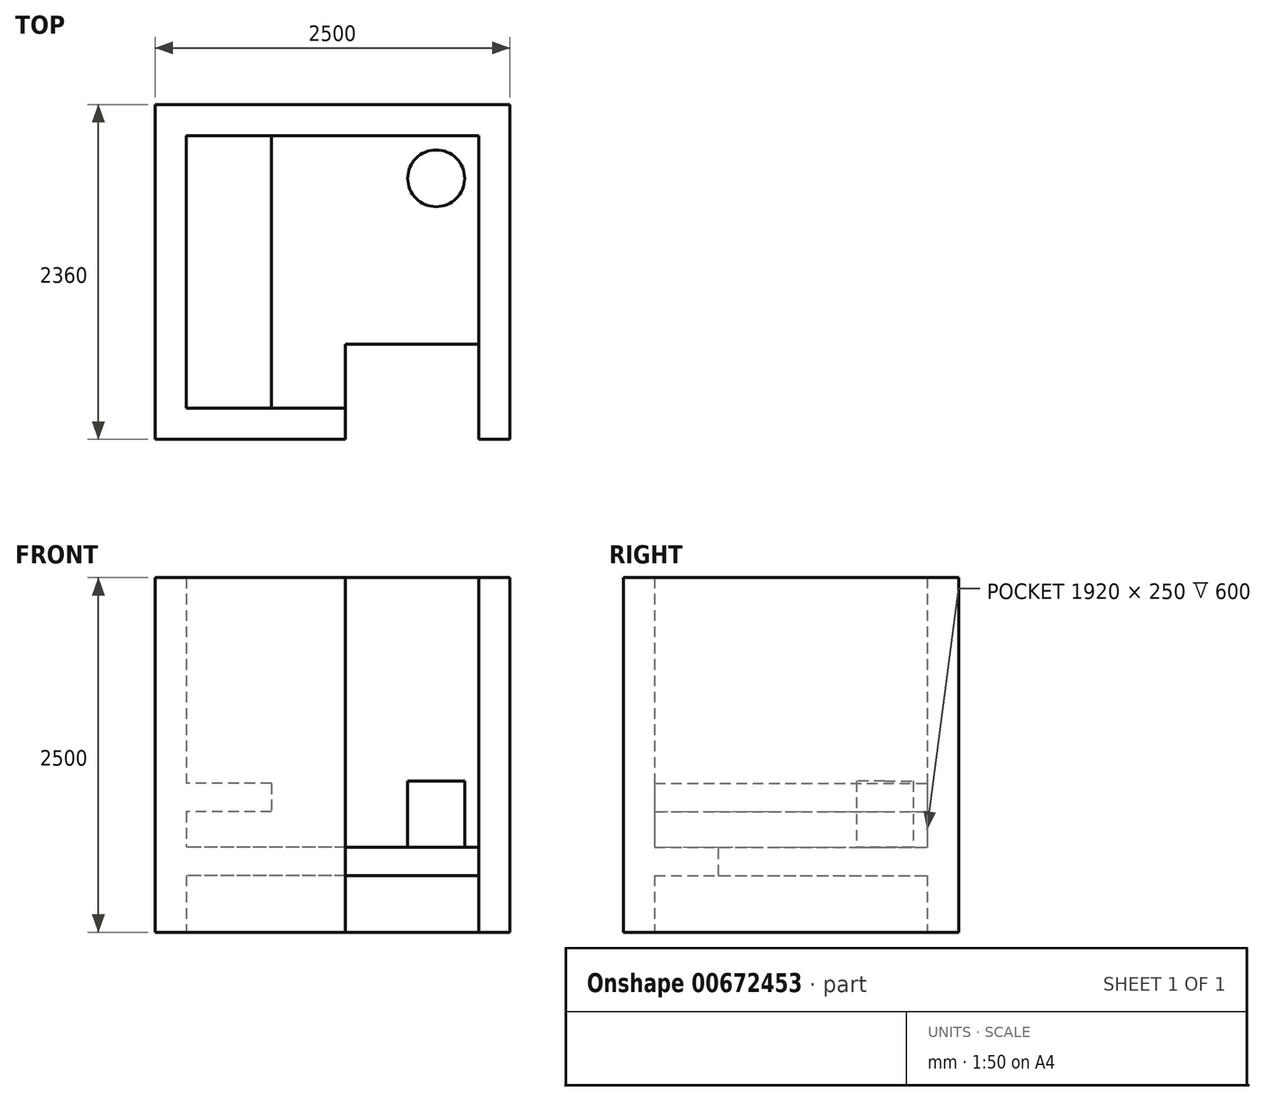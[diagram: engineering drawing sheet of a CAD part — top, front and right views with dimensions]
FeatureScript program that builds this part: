
annotation { "Feature Type Name" : "Feature", "Feature Type Description" : "" }
export const myFeature = defineFeature(function(context is Context, id is Id, definition is map)
    precondition{}
    {
        {
            var Q0;
            Q0=qCreatedBy(makeId("Top.planeOp"),FACE);
            var sketch = newSketch(context, id + "F0", { "sketchPlane" : qUnion([Q0])});
            skLineSegment(sketch, "E0.bottom", {"start": v(1030, 960) * mm, "end": v(-1030, 960) * mm});
            skLineSegment(sketch, "E0.top", {"start": v(90, -960) * mm, "end": v(-1030, -960) * mm});
            skLineSegment(sketch, "E0.left", {"start": v(1030, 960) * mm, "end": v(1030, -960) * mm});
            skLineSegment(sketch, "E0.right", {"start": v(-1030, 960) * mm, "end": v(-1030, -960) * mm});
            skPoint(sketch, "E0.middle", {"position": v(0, 0) * mm});
            skLineSegment(sketch, "E1.0", {"start": v(1250, 1180) * mm, "end": v(-1250, 1180) * mm});
            skLineSegment(sketch, "E1.1", {"start": v(1250, 1180) * mm, "end": v(1250, -1180) * mm});
            skLineSegment(sketch, "E1.2", {"start": v(1250, -1180) * mm, "end": v(1030, -1180) * mm});
            skLineSegment(sketch, "E1.3", {"start": v(-1250, 1180) * mm, "end": v(-1250, -1180) * mm});
            skLineSegment(sketch, "E2", {"start": v(1030, -960) * mm, "end": v(1030, -1180) * mm});
            skLineSegment(sketch, "E3", {"start": v(90, -960) * mm, "end": v(90, -1180) * mm});
            skLineSegment(sketch, "E4.trimOffspring", {"start": v(90, -1180) * mm, "end": v(-1250, -1180) * mm});
            skSolve(sketch);
        }
        {
            var Q0;
            Q0=makeQuery(id+"F0.imprint","IMPRINT",FACE,{"disambiguationData":[TD([[makeQuery(id+"F0.imprint","IMPRINT",EDGE,{"derivedFrom":sQuery(id+"F0.wireOp",EDGE,"E0.bottom")}),-1.0]])]});
            extrude(context, id + "F1", {"entities" : qUnion([Q0]), "depth" : 2500 * mm, "offsetDistance" : 25 * mm});
        }
        {
            var Q0;
            Q0=makeQuery(id+"F1.opExtrude","SWEPT_FACE",FACE,{"disambiguationData":[OSD([sQuery(id+"F0.wireOp",EDGE,"E0.bottom")])]});
            var sketch = newSketch(context, id + "F2", { "sketchPlane" : qUnion([Q0])});
            skLineSegment(sketch, "E5.bottom", {"start": v(1030, 600) * mm, "end": v(-1030, 600) * mm});
            skLineSegment(sketch, "E5.top", {"start": v(1030, 400) * mm, "end": v(-1030, 400) * mm});
            skLineSegment(sketch, "E5.left", {"start": v(1030, 600) * mm, "end": v(1030, 400) * mm});
            skLineSegment(sketch, "E5.right", {"start": v(-1030, 600) * mm, "end": v(-1030, 400) * mm});
            skSolve(sketch);
        }
        {
            var Q0;
            Q0=makeQuery(id+"F2.imprint","IMPRINT",FACE,{"disambiguationData":[TD([[makeQuery(id+"F2.imprint","IMPRINT",EDGE,{"derivedFrom":sQuery(id+"F2.wireOp",EDGE,"E5.bottom")}),1.0]])]});
            extrude(context, id + "F3", {"entities" : qUnion([Q0]), "operationType" : NewBodyOperationType.ADD, "depth" : 1920 * mm, "offsetDistance" : 25 * mm});
        }
        {
            var Q0;
            {var subQ1=sQuery(id+"F0.wireOp",EDGE,"E0.right");Q0=makeQuery(id+"F3.boolean.opBoolean","SPLIT",FACE,{"disambiguationData":[TD([makeQuery(id+"F3.opExtrude","SWEPT_FACE",FACE,{"disambiguationData":[OSD([sQuery(id+"F2.wireOp",EDGE,"E5.bottom")])]})])],"derivedFrom":makeQuery(id+"F1.opExtrude","SWEPT_FACE",FACE,{"disambiguationData":[OSD([subQ1])]})});}
            var sketch = newSketch(context, id + "F4", { "sketchPlane" : qUnion([Q0])});
            skLineSegment(sketch, "E6.bottom", {"start": v(-960, 1050) * mm, "end": v(960, 1050) * mm});
            skLineSegment(sketch, "E6.top", {"start": v(-960, 850) * mm, "end": v(960, 850) * mm});
            skLineSegment(sketch, "E6.left", {"start": v(-960, 1050) * mm, "end": v(-960, 850) * mm});
            skLineSegment(sketch, "E6.right", {"start": v(960, 1050) * mm, "end": v(960, 850) * mm});
            skSolve(sketch);
        }
        {
            var Q0;
            Q0 = qSketchRegion(id + "F4", true);
            extrude(context, id + "F5", {"entities" : qUnion([Q0]), "operationType" : NewBodyOperationType.ADD, "depth" : 600 * mm, "offsetDistance" : 25 * mm});
        }
        {
            var Q0;
            Q0=makeQuery(id+"F3.opExtrude","SWEPT_FACE",FACE,{"disambiguationData":[OSD([sQuery(id+"F2.wireOp",EDGE,"E5.bottom")])]});
            var sketch = newSketch(context, id + "F6", { "sketchPlane" : qUnion([Q0])});
            skCircle(sketch, "E7", {"center": v(730, 660) * mm, "radius": 200 * mm});
            skSolve(sketch);
        }
        {
            var Q0;
            Q0 = qSketchRegion(id + "F6", true);
            extrude(context, id + "F7", {"entities" : qUnion([Q0]), "operationType" : NewBodyOperationType.ADD, "depth" : 465 * mm, "offsetDistance" : 25 * mm});
        }
        {
            var Q0;
            Q0=makeQuery(id+"F3.opExtrude","SWEPT_FACE",FACE,{"disambiguationData":[OSD([sQuery(id+"F2.wireOp",EDGE,"E5.bottom")])]});
            var sketch = newSketch(context, id + "F8", { "sketchPlane" : qUnion([Q0])});
            skLineSegment(sketch, "E8.bottom", {"start": v(90, -960) * mm, "end": v(1030, -960) * mm});
            skLineSegment(sketch, "E8.top", {"start": v(90, -510) * mm, "end": v(1030, -510) * mm});
            skLineSegment(sketch, "E8.left", {"start": v(90, -960) * mm, "end": v(90, -510) * mm});
            skLineSegment(sketch, "E8.right", {"start": v(1030, -960) * mm, "end": v(1030, -510) * mm});
            skSolve(sketch);
        }
        {
            var Q0;
            Q0 = qSketchRegion(id + "F8", true);
            extrude(context, id + "F9", {"entities" : qUnion([Q0]), "operationType" : NewBodyOperationType.REMOVE, "endBound" : BoundingType.UP_TO_NEXT, "oppositeDirection" : true, "depth" : 25 * mm, "offsetDistance" : 25 * mm});
        }
        {
            var Q0;
            Q0=makeQuery(id+"F1.opExtrude","SWEPT_FACE",FACE,{"disambiguationData":[OSD([sQuery(id+"F0.wireOp",EDGE,"E1.3")])]});
            var sketch = newSketch(context, id + "F10", { "sketchPlane" : qUnion([Q0])});
            skLineSegment(sketch, "E9.bottom", {"start": v(0, 1548.4) * mm, "end": v(-467.6, 1548.4) * mm});
            skLineSegment(sketch, "E9.top", {"start": v(0, 1298.52) * mm, "end": v(-467.6, 1298.52) * mm});
            skLineSegment(sketch, "E9.left", {"start": v(0, 1548.4) * mm, "end": v(0, 1298.52) * mm});
            skLineSegment(sketch, "E9.right", {"start": v(-467.6, 1548.4) * mm, "end": v(-467.6, 1298.52) * mm});
            skSolve(sketch);
        }
        {
            var Q0;
            Q0=sQuery(id+"F10.wireOp",EDGE,"E9.top");
            var Q1;
            Q1=sQuery(id+"F10.wireOp",EDGE,"E9.bottom");
            var Q2;
            Q2=sQuery(id+"F10.wireOp",EDGE,"E9.right");
            extrude(context, id + "F11", {"bodyType" : ToolBodyType.SURFACE, "surfaceEntities" : qUnion([Q0, Q1, Q2]), "depth" : 25 * mm, "offsetDistance" : 25 * mm});
        }
    });
